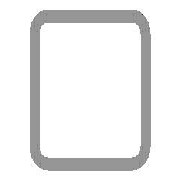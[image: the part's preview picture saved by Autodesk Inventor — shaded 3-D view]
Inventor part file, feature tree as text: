
AUTODESK INVENTOR PART (.ipt)
format: ipt  version: 2025 (Build 290162010, 162A)  size: 168,960 bytes
history: native  units: mm (DEFAULTED — no unit token found)
features: other x3, sketch x3, projected_geometry x2, extrude x1, plane x1
ambient origin geometry x8: Origin, YZ Plane, XZ Plane, XY Plane, X Axis, Y Axis, Z Axis, Center Point
bodies: Solid1 (feature_tree), Body (feature_tree)
feature tree (10):
  other  "Driven Length"
  other  "Start plane"
  other  "End plane"
  sketch  "Sketch5"  dims[d7=6.0mm]
  extrude  "Extrusion2"  TaperAngle=0.0deg  [1 undecoded]
  sketch  "Sketch3"  dims[d3=1000.0mm d4=0.0mm]
  plane  "Work Plane3"
  sketch  "Sketch6"  dims[d9=80.0mm d11=80.0mm d12=3.0mm d13=-0.0mm d14=1000.0mm d15=40.0mm d16=40.0mm d17=90.0deg d18=1000.0mm d22=300.0mm d24=940.0mm d25=89.3mm d26=40.0mm d27=940.0mm d28=300.0mm d30=349.157702mm d31=0.0mm d32=0.0mm d33=10.0mm]
  projected_geometry  "Projected Loop1"
  projected_geometry  "Projected Loop2"
note: 1 required parameter value undecoded (feature->parameter linkage not recoverable at this tier; creation-order binding heuristic only, values carry confidence <= 0.55)
